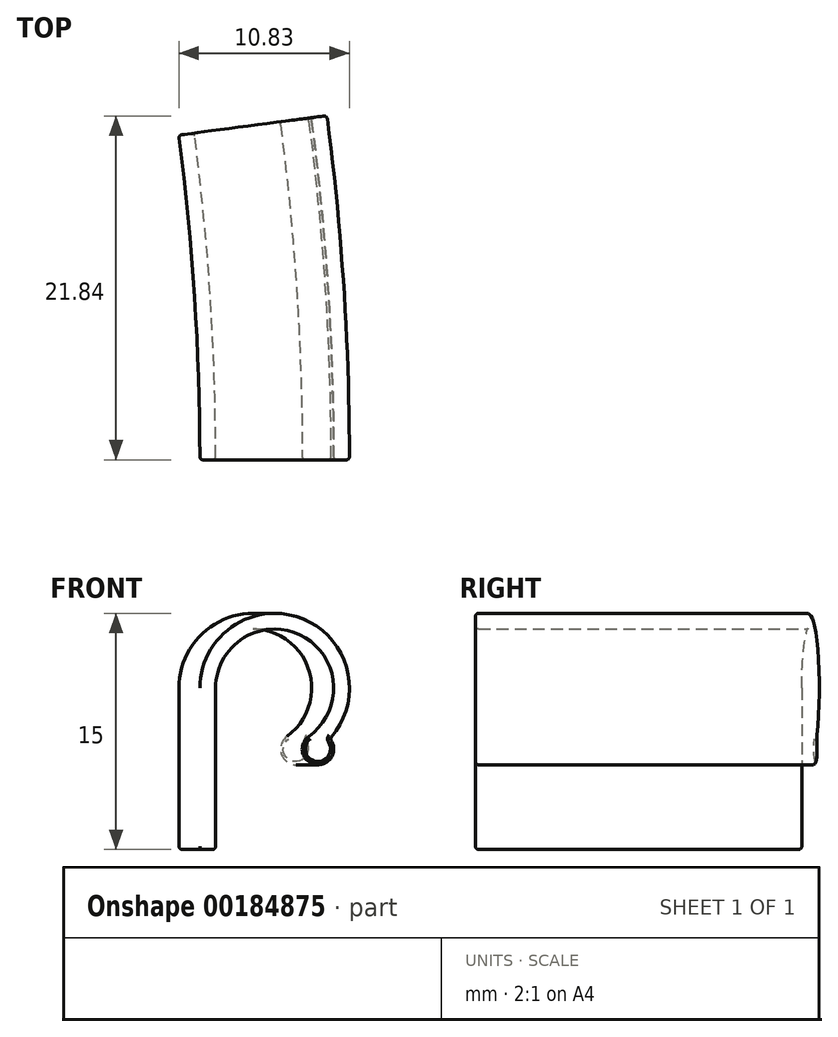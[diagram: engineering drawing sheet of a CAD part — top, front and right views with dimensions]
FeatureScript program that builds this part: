
annotation { "Feature Type Name" : "Feature", "Feature Type Description" : "" }
export const myFeature = defineFeature(function(context is Context, id is Id, definition is map)
    precondition{}
    {
        {
            var Q0;
            Q0=qCreatedBy(makeId("Front.planeOp"),FACE);
            var sketch = newSketch(context, id + "F0", { "sketchPlane" : qUnion([Q0])});
            skLineSegment(sketch, "E0", {"start": v(0, 0) * mm, "end": v(0, 10.25) * mm});
            skArc(sketch, "E1", {"start": v(0, 10.25) * mm, "mid": v(5.47, 13.58) * mm, "end": v(5.92, 7.2) * mm});
            skArc(sketch, "E2", {"start": v(5.92, 7.2) * mm, "mid": v(6.39, 5.38) * mm, "end": v(7.25, 7.04) * mm});
            skLineSegment(sketch, "E3", {"start": v(0, 0) * mm, "end": v(-1, 0) * mm});
            skLineSegment(sketch, "E4", {"start": v(-1, 0) * mm, "end": v(-1, 10.25) * mm});
            skArc(sketch, "E5", {"start": v(-1, 10.25) * mm, "mid": v(5.47, 14.68) * mm, "end": v(7.25, 7.04) * mm});
            skLineSegment(sketch, "E6", {"start": v(-159, 0) * mm, "end": v(-159, 10.25) * mm});
            skSolve(sketch);
        }
        {
            var Q0;
            Q0=makeQuery(id+"F0.imprint","IMPRINT",FACE,{"disambiguationData":[TD([[makeQuery(id+"F0.imprint","IMPRINT",EDGE,{"derivedFrom":sQuery(id+"F0.wireOp",EDGE,"E0")}),1.0]])]});
            var Q1;
            Q1=sQuery(id+"F0.wireOp",EDGE,"E6");
            revolve(context, id + "F1", {"entities" : qUnion([Q0]), "axis" : qUnion([Q1]), "revolveType" : RevolveType.ONE_DIRECTION, "angle" : 7.5 * degree});
        }
        {
            var Q0;
            Q0=makeQuery(id+"F1.opRevolve","SWEPT_EDGE",EDGE,{"disambiguationData":[OSD([sQuery(id+"F0.wireOp",EDGE,"E3"),sQuery(id+"F0.wireOp",EDGE,"E4")])]});
            var Q1;
            Q1=makeQuery(id+"F1.opRevolve","SWEPT_EDGE",EDGE,{"disambiguationData":[OSD([sQuery(id+"F0.wireOp",EDGE,"E0"),sQuery(id+"F0.wireOp",EDGE,"E3")])]});
            var Q2;
            Q2=makeQuery(id+"F1.opRevolve","CAP_EDGE",EDGE,{"disambiguationData":[OSD([sQuery(id+"F0.wireOp",EDGE,"E4")])],"isStart":true});
            var Q3;
            Q3=makeQuery(id+"F1.opRevolve","CAP_EDGE",EDGE,{"disambiguationData":[OSD([sQuery(id+"F0.wireOp",EDGE,"E0")])],"isStart":true});
            var Q4;
            Q4=makeQuery(id+"F1.opRevolve","CAP_EDGE",EDGE,{"disambiguationData":[OSD([sQuery(id+"F0.wireOp",EDGE,"E3")])],"isStart":true});
            var Q5;
            Q5=makeQuery(id+"F1.opRevolve","CAP_EDGE",EDGE,{"disambiguationData":[OSD([sQuery(id+"F0.wireOp",EDGE,"E3")])],"isStart":false});
            var Q6;
            Q6=makeQuery(id+"F1.opRevolve","SWEPT_EDGE",EDGE,{"disambiguationData":[OSD([sQuery(id+"F0.wireOp",EDGE,"E2"),sQuery(id+"F0.wireOp",EDGE,"E5")])]});
            var Q7;
            Q7=makeQuery(id+"F1.opRevolve","CAP_EDGE",EDGE,{"disambiguationData":[OSD([sQuery(id+"F0.wireOp",EDGE,"E0")])],"isStart":false});
            var Q8;
            Q8=makeQuery(id+"F1.opRevolve","CAP_EDGE",EDGE,{"disambiguationData":[OSD([sQuery(id+"F0.wireOp",EDGE,"E4")])],"isStart":false});
            fillet(context, id + "F2", {"entities" : qUnion([Q0, Q1, Q2, Q3, Q4, Q5, Q6, Q7, Q8]), "radius" : 0.2 * mm, "tangentPropagation" : true, "allowEdgeOverflow" : false});
        }
    });
